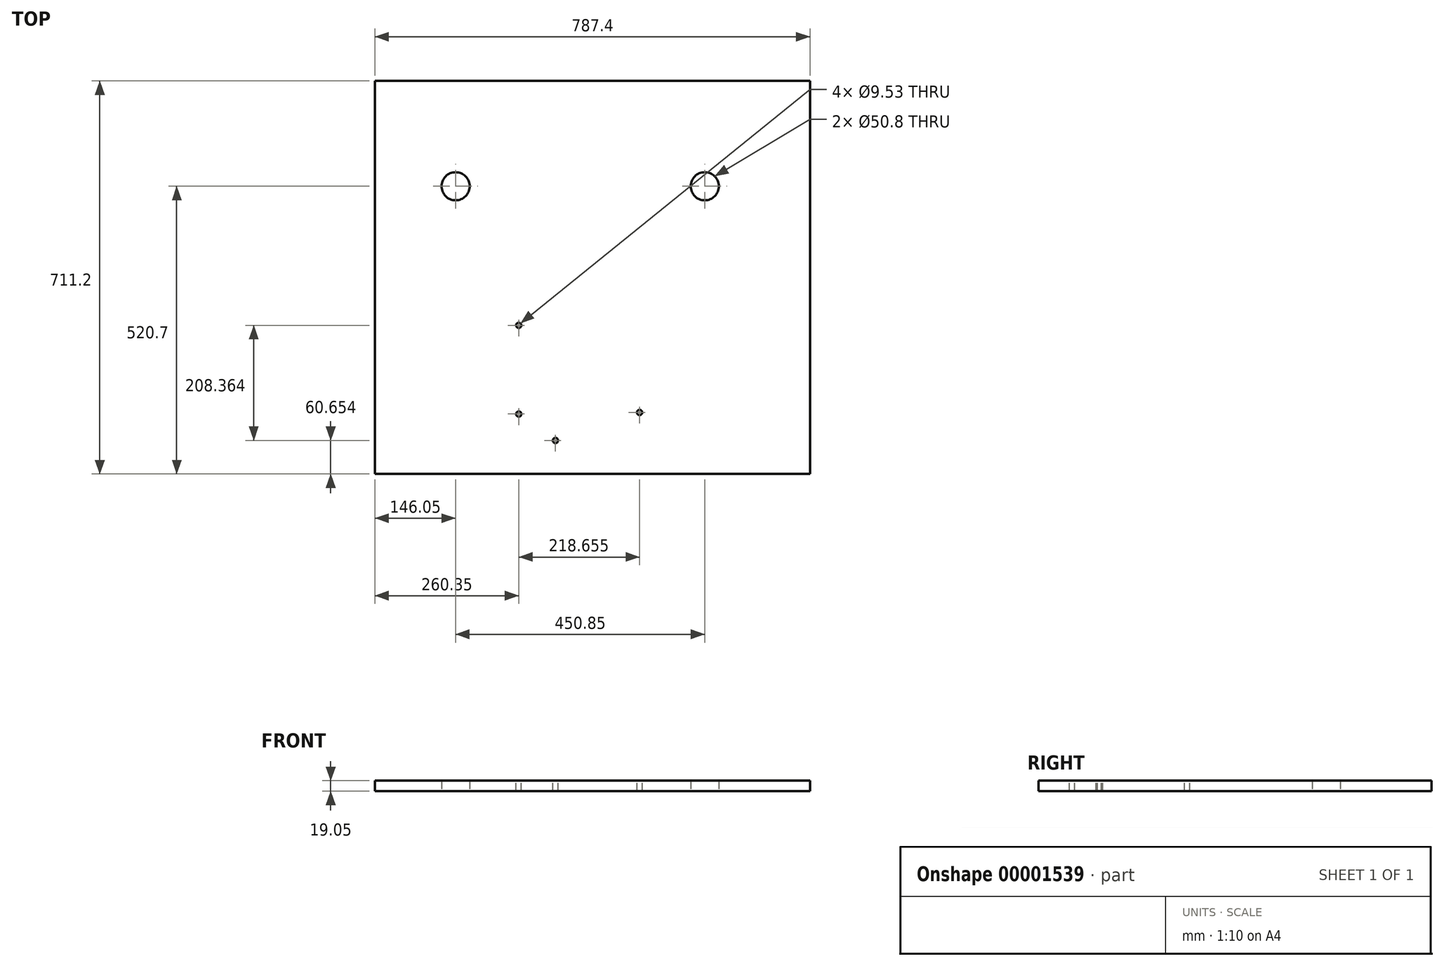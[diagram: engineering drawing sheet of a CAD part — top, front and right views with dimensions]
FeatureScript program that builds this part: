
annotation { "Feature Type Name" : "Feature", "Feature Type Description" : "" }
export const myFeature = defineFeature(function(context is Context, id is Id, definition is map)
    precondition{}
    {
        {
            var Q0;
            Q0=qCreatedBy(makeId("Top.planeOp"),FACE);
            var sketch = newSketch(context, id + "F0", { "sketchPlane" : qUnion([Q0])});
            skLineSegment(sketch, "E0.bottom", {"start": v(-393.7, 355.6) * mm, "end": v(393.7, 355.6) * mm});
            skLineSegment(sketch, "E0.top", {"start": v(-393.7, -355.6) * mm, "end": v(393.7, -355.6) * mm});
            skLineSegment(sketch, "E0.left", {"start": v(-393.7, 355.6) * mm, "end": v(-393.7, -355.6) * mm});
            skLineSegment(sketch, "E0.right", {"start": v(393.7, 355.6) * mm, "end": v(393.7, -355.6) * mm});
            skCircle(sketch, "E1", {"center": v(-247.65, 165.1) * mm, "radius": 25.4 * mm});
            skCircle(sketch, "E2", {"center": v(203.2, 165.1) * mm, "radius": 25.4 * mm});
            skSolve(sketch);
        }
        {
            var Q0;
            Q0=makeQuery(id+"F0.imprint","IMPRINT",FACE,{"disambiguationData":[TD([[makeQuery(id+"F0.imprint","IMPRINT",EDGE,{"derivedFrom":sQuery(id+"F0.wireOp",EDGE,"E0.bottom")}),-1.0]])]});
            extrude(context, id + "F1", {"entities" : qUnion([Q0]), "depth" : 19.05 * mm});
        }
        {
            var Q0;
            Q0=makeQuery(id+"F1.opExtrude","CAP_FACE",FACE,{"disambiguationData":[OSD([sQuery(id+"F0.wireOp",EDGE,"E0.bottom"),sQuery(id+"F0.wireOp",EDGE,"E0.top"),sQuery(id+"F0.wireOp",EDGE,"E0.left"),sQuery(id+"F0.wireOp",EDGE,"E0.right"),sQuery(id+"F0.wireOp",EDGE,"E1"),sQuery(id+"F0.wireOp",EDGE,"E2")])],"isStart":false});
            var sketch = newSketch(context, id + "F2", { "sketchPlane" : qUnion([Q0])});
            skLineSegment(sketch, "E3", {"start": v(-165.1, -24.53) * mm, "end": v(154.2, -254.85) * mm, "construction": true});
            skLineSegment(sketch, "E4", {"start": v(-165.1, -263.33) * mm, "end": v(-72.4, -330.2) * mm, "construction": true});
            skLineSegment(sketch, "E5", {"start": v(-5.45, -139.7) * mm, "end": v(-180.77, -382.75) * mm, "construction": true});
            skLineSegment(sketch, "E6", {"start": v(-165.1, -24.53) * mm, "end": v(-165.1, -263.33) * mm, "construction": true});
            skLineSegment(sketch, "E7", {"start": v(-72.4, -330.2) * mm, "end": v(154.2, -254.85) * mm, "construction": true});
            skLineSegment(sketch, "E8.0", {"start": v(-133.35, -86.58) * mm, "end": v(85.3, -244.3) * mm, "construction": true});
            skLineSegment(sketch, "E8.1", {"start": v(-133.35, -86.58) * mm, "end": v(-133.35, -247.09) * mm, "construction": true});
            skLineSegment(sketch, "E8.2", {"start": v(-133.35, -247.09) * mm, "end": v(-67, -294.95) * mm, "construction": true});
            skLineSegment(sketch, "E8.3", {"start": v(-67, -294.95) * mm, "end": v(85.3, -244.3) * mm, "construction": true});
            skCircle(sketch, "E9", {"center": v(-133.35, -86.58) * mm, "radius": 4.76 * mm});
            skCircle(sketch, "E10", {"center": v(85.3, -244.3) * mm, "radius": 4.76 * mm});
            skCircle(sketch, "E11", {"center": v(-67, -294.95) * mm, "radius": 4.76 * mm});
            skCircle(sketch, "E12", {"center": v(-133.35, -247.09) * mm, "radius": 4.76 * mm});
            skSolve(sketch);
        }
        {
            var Q0;
            {Q0=qUnion([makeQuery(id+"F2.imprint","IMPRINT",FACE,{"disambiguationData":[TD([[makeQuery(id+"F2.imprint","IMPRINT",EDGE,{"derivedFrom":sQuery(id+"F2.wireOp",EDGE,"E9")}),1.0]])]}),makeQuery(id+"F2.imprint","IMPRINT",FACE,{"disambiguationData":[TD([[makeQuery(id+"F2.imprint","IMPRINT",EDGE,{"derivedFrom":sQuery(id+"F2.wireOp",EDGE,"E10")}),1.0]])]}),makeQuery(id+"F2.imprint","IMPRINT",FACE,{"disambiguationData":[TD([[makeQuery(id+"F2.imprint","IMPRINT",EDGE,{"derivedFrom":sQuery(id+"F2.wireOp",EDGE,"E11")}),1.0]])]}),makeQuery(id+"F2.imprint","IMPRINT",FACE,{"disambiguationData":[TD([[makeQuery(id+"F2.imprint","IMPRINT",EDGE,{"derivedFrom":sQuery(id+"F2.wireOp",EDGE,"E12")}),1.0]])]})]);}
            extrude(context, id + "F3", {"entities" : qUnion([Q0]), "operationType" : NewBodyOperationType.REMOVE, "endBound" : BoundingType.THROUGH_ALL, "oppositeDirection" : true, "depth" : 25.4 * mm});
        }
    });
